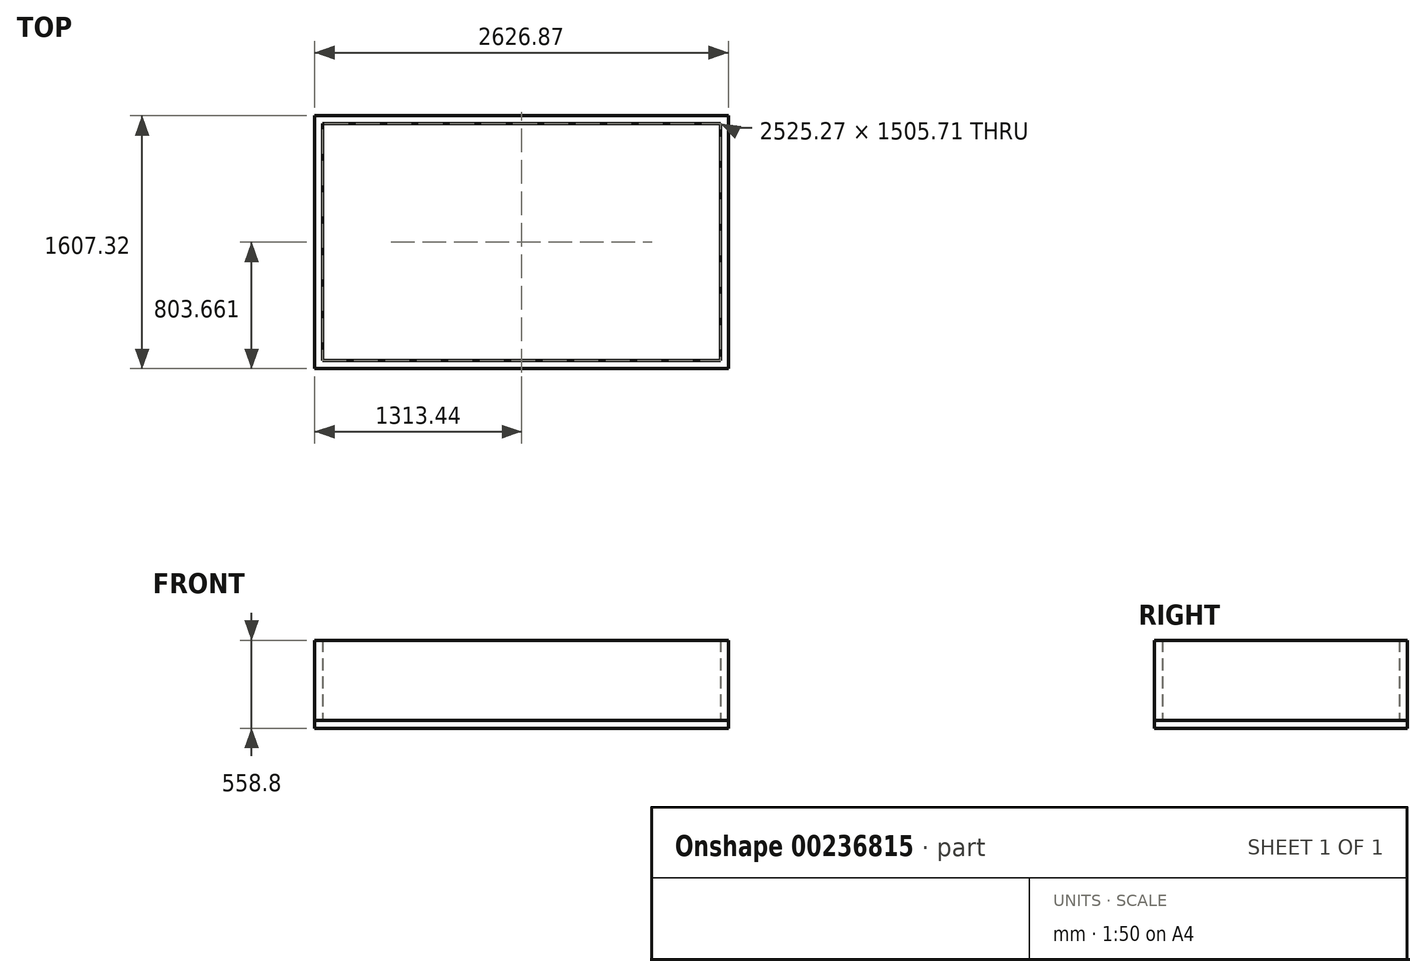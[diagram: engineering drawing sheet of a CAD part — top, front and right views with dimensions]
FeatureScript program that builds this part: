
annotation { "Feature Type Name" : "Feature", "Feature Type Description" : "" }
export const myFeature = defineFeature(function(context is Context, id is Id, definition is map)
    precondition{}
    {
        {
            var Q0;
            Q0=qCreatedBy(makeId("Top.planeOp"),FACE);
            var sketch = newSketch(context, id + "F0", { "sketchPlane" : qUnion([Q0])});
            skLineSegment(sketch, "E0.bottom", {"start": v(-1311.49, 762.97) * mm, "end": v(1315.38, 762.97) * mm});
            skLineSegment(sketch, "E0.top", {"start": v(-1311.49, -844.35) * mm, "end": v(1315.38, -844.35) * mm});
            skLineSegment(sketch, "E0.left", {"start": v(-1311.49, 762.97) * mm, "end": v(-1311.49, -844.35) * mm});
            skLineSegment(sketch, "E0.right", {"start": v(1315.38, 762.97) * mm, "end": v(1315.38, -844.35) * mm});
            skSolve(sketch);
        }
        {
            var Q0;
            Q0=makeQuery(id+"F0.imprint","IMPRINT",FACE,{"disambiguationData":[TD([[makeQuery(id+"F0.imprint","IMPRINT",EDGE,{"derivedFrom":sQuery(id+"F0.wireOp",EDGE,"E0.bottom")}),-1.0]])]});
            extrude(context, id + "F1", {"entities" : qUnion([Q0]), "depth" : 50.8 * mm});
        }
        {
            var Q0;
            Q0=makeQuery(id+"F1.opExtrude","CAP_FACE",FACE,{"disambiguationData":[OSD([sQuery(id+"F0.wireOp",EDGE,"E0.bottom"),sQuery(id+"F0.wireOp",EDGE,"E0.top"),sQuery(id+"F0.wireOp",EDGE,"E0.left"),sQuery(id+"F0.wireOp",EDGE,"E0.right")])],"isStart":false});
            var sketch = newSketch(context, id + "F2", { "sketchPlane" : qUnion([Q0])});
            skLineSegment(sketch, "E1.0", {"start": v(-1260.69, 712.17) * mm, "end": v(-1260.69, -793.55) * mm});
            skLineSegment(sketch, "E2.0", {"start": v(-1260.69, 712.17) * mm, "end": v(1264.58, 712.17) * mm});
            skLineSegment(sketch, "E3.0", {"start": v(1264.58, 712.17) * mm, "end": v(1264.58, -793.55) * mm});
            skLineSegment(sketch, "E4.0", {"start": v(-1260.69, -793.55) * mm, "end": v(1264.58, -793.55) * mm});
            skSolve(sketch);
        }
        {
            var Q0;
            Q0=makeQuery(id+"F2.imprint","IMPRINT",FACE,{"disambiguationData":[TD([[makeQuery(id+"F2.imprint","IMPRINT",EDGE,{"derivedFrom":sQuery(id+"F2.wireOp",EDGE,"E1.0")}),-1.0]])]});
            extrude(context, id + "F3", {"entities" : qUnion([Q0]), "depth" : 508 * mm});
        }
    });
